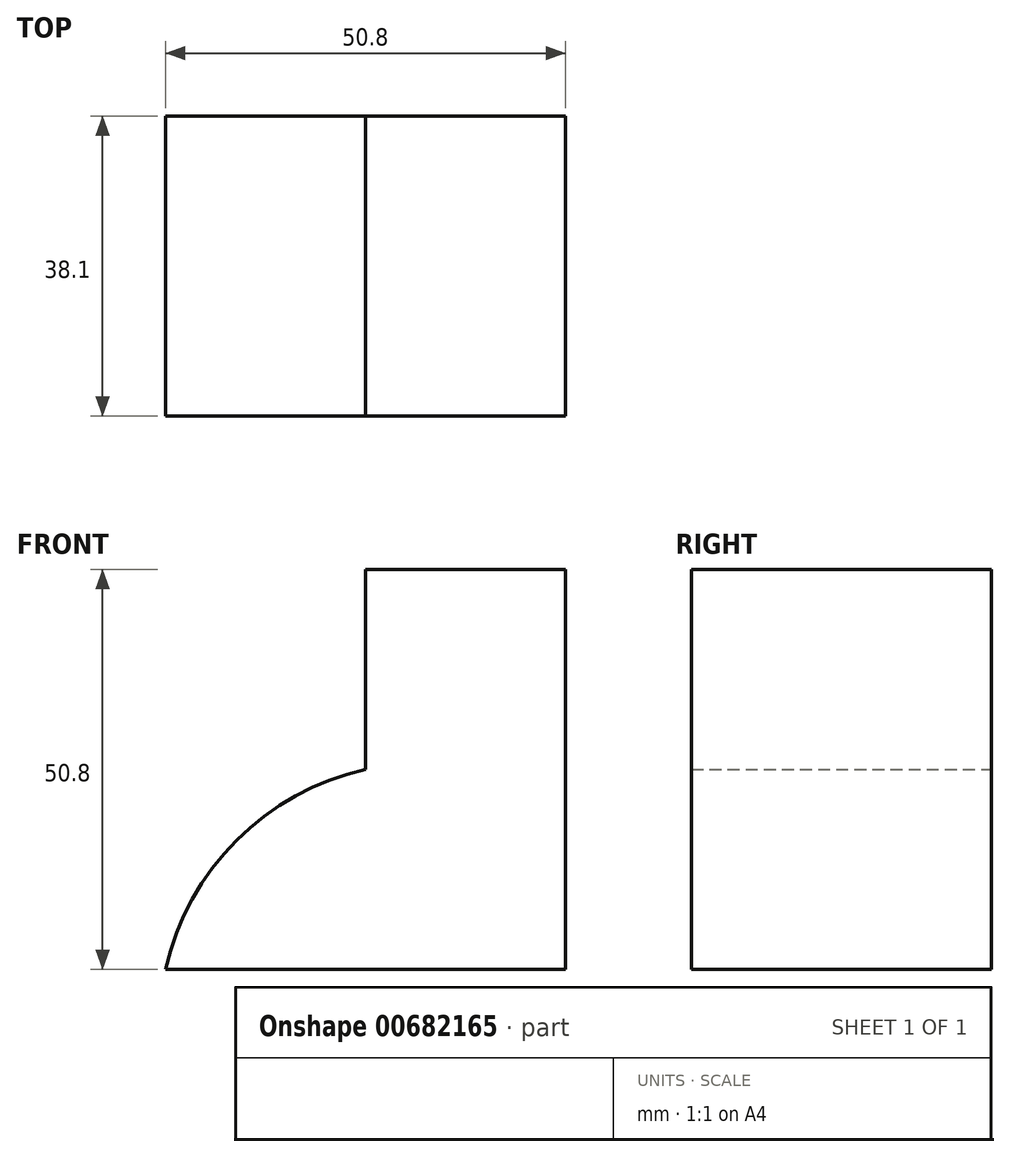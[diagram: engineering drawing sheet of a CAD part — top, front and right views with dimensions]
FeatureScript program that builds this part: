
annotation { "Feature Type Name" : "Feature", "Feature Type Description" : "" }
export const myFeature = defineFeature(function(context is Context, id is Id, definition is map)
    precondition{}
    {
        {
            var Q0;
            Q0=qCreatedBy(makeId("Front.planeOp"),FACE);
            var sketch = newSketch(context, id + "F0", { "sketchPlane" : qUnion([Q0])});
            skLineSegment(sketch, "E0", {"start": v(-34.11, -32.38) * mm, "end": v(16.69, -32.38) * mm});
            skLineSegment(sketch, "E1", {"start": v(16.69, -32.38) * mm, "end": v(16.69, 18.42) * mm});
            skLineSegment(sketch, "E2", {"start": v(16.69, 18.42) * mm, "end": v(-8.71, 18.42) * mm});
            skLineSegment(sketch, "E3", {"start": v(-8.71, 18.42) * mm, "end": v(-8.71, -6.98) * mm});
            skArc(sketch, "E4", {"start": v(-8.71, -6.98) * mm, "mid": v(-25.1, -15.99) * mm, "end": v(-34.11, -32.38) * mm});
            skSolve(sketch);
        }
        {
            var Q0;
            Q0=makeQuery(id+"F0.imprint","IMPRINT",FACE,{"disambiguationData":[TD([[makeQuery(id+"F0.imprint","IMPRINT",EDGE,{"derivedFrom":sQuery(id+"F0.wireOp",EDGE,"E0")}),1.0]])]});
            extrude(context, id + "F1", {"entities" : qUnion([Q0]), "depth" : 38.1 * mm, "offsetDistance" : 25.4 * mm});
        }
    });
